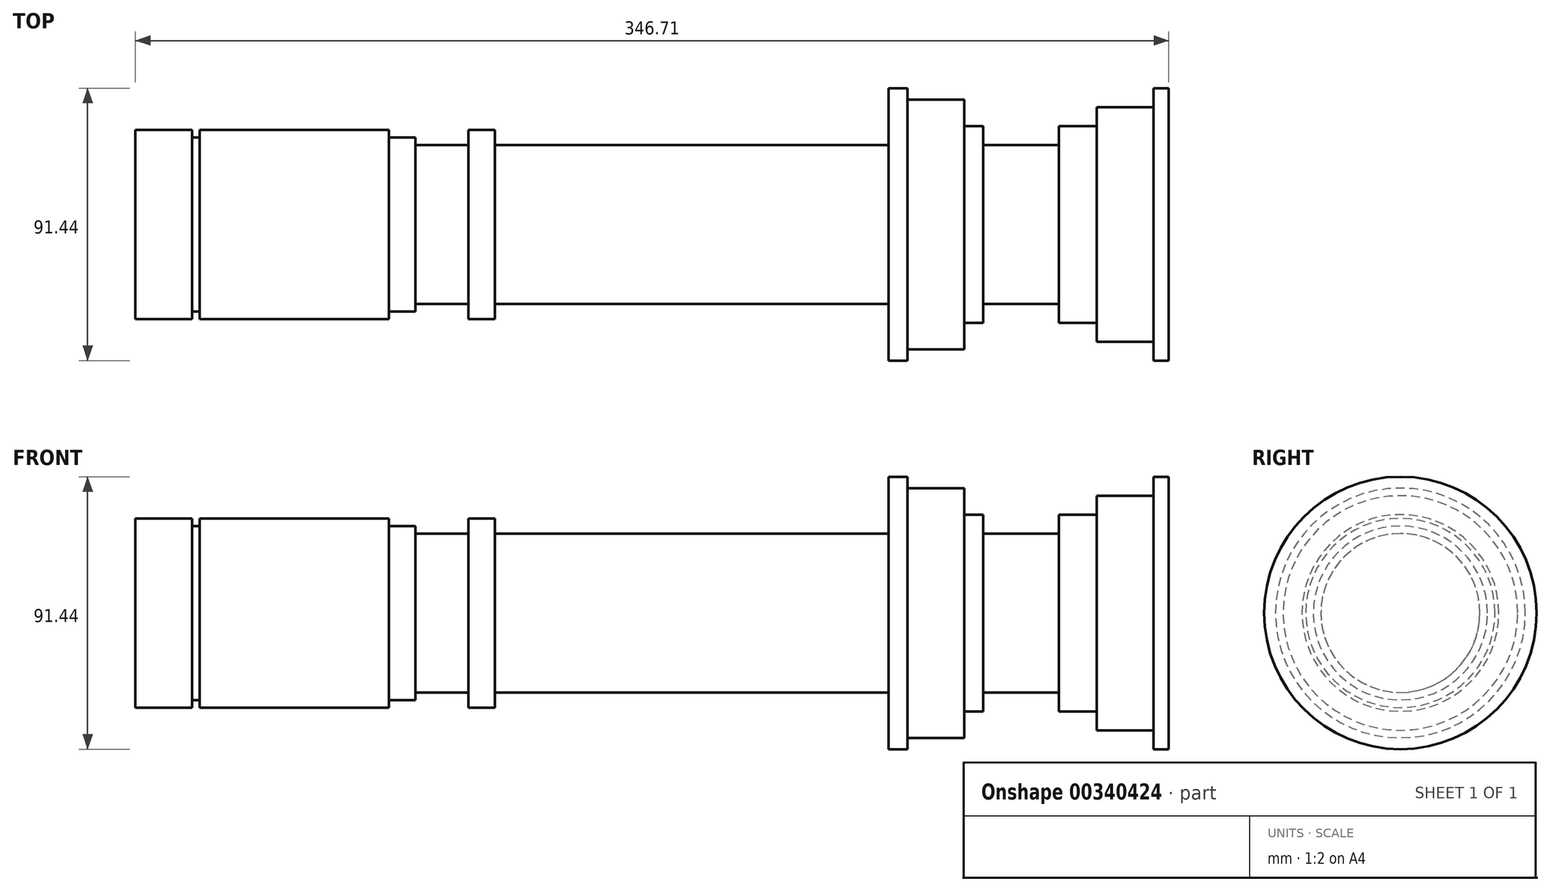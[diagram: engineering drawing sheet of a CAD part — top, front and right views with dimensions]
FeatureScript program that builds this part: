
annotation { "Feature Type Name" : "Feature", "Feature Type Description" : "" }
export const myFeature = defineFeature(function(context is Context, id is Id, definition is map)
    precondition{}
    {
        {
            var Q0;
            Q0=qCreatedBy(makeId("Front.planeOp"),FACE);
            var sketch = newSketch(context, id + "F0", { "sketchPlane" : qUnion([Q0])});
            skLineSegment(sketch, "E0", {"start": v(0, 31.75) * mm, "end": v(19.05, 31.75) * mm});
            skLineSegment(sketch, "E1", {"start": v(19.05, 31.75) * mm, "end": v(19.05, 29.21) * mm});
            skLineSegment(sketch, "E2", {"start": v(19.05, 29.21) * mm, "end": v(21.6, 29.21) * mm});
            skLineSegment(sketch, "E3", {"start": v(21.59, 29.21) * mm, "end": v(21.59, 31.75) * mm});
            skLineSegment(sketch, "E4", {"start": v(21.6, 31.75) * mm, "end": v(85.1, 31.75) * mm});
            skLineSegment(sketch, "E5", {"start": v(85.1, 31.75) * mm, "end": v(85.1, 29.21) * mm});
            skLineSegment(sketch, "E6", {"start": v(85.1, 29.21) * mm, "end": v(93.98, 29.21) * mm});
            skLineSegment(sketch, "E7", {"start": v(93.98, 29.21) * mm, "end": v(93.98, 26.67) * mm});
            skLineSegment(sketch, "E8", {"start": v(93.98, 26.67) * mm, "end": v(100.33, 26.67) * mm});
            skLineSegment(sketch, "E9", {"start": v(259.08, 45.72) * mm, "end": v(252.73, 45.72) * mm});
            skLineSegment(sketch, "E10", {"start": v(259.08, 41.9) * mm, "end": v(259.08, 45.72) * mm});
            skLineSegment(sketch, "E11", {"start": v(259.08, 41.9) * mm, "end": v(278.13, 41.9) * mm});
            skLineSegment(sketch, "E12", {"start": v(278.13, 41.9) * mm, "end": v(278.13, 33.02) * mm});
            skLineSegment(sketch, "E13", {"start": v(278.13, 33.02) * mm, "end": v(284.48, 33.02) * mm});
            skLineSegment(sketch, "E14", {"start": v(284.48, 33.02) * mm, "end": v(284.48, 26.67) * mm});
            skLineSegment(sketch, "E15", {"start": v(284.48, 26.67) * mm, "end": v(309.88, 26.67) * mm});
            skLineSegment(sketch, "E16", {"start": v(309.88, 26.67) * mm, "end": v(309.88, 33.02) * mm});
            skLineSegment(sketch, "E17", {"start": v(309.88, 33.02) * mm, "end": v(322.58, 33.02) * mm});
            skLineSegment(sketch, "E18", {"start": v(322.58, 33.02) * mm, "end": v(322.58, 39.37) * mm});
            skLineSegment(sketch, "E19", {"start": v(322.58, 39.37) * mm, "end": v(341.63, 39.37) * mm});
            skLineSegment(sketch, "E20", {"start": v(341.63, 39.37) * mm, "end": v(341.63, 45.72) * mm});
            skLineSegment(sketch, "E21", {"start": v(341.63, 45.72) * mm, "end": v(346.71, 45.72) * mm});
            skLineSegment(sketch, "E22", {"start": v(346.71, 45.72) * mm, "end": v(346.71, 0) * mm});
            skLineSegment(sketch, "E23", {"start": v(346.7, 0) * mm, "end": v(0, 0) * mm});
            skLineSegment(sketch, "E24", {"start": v(0, 0) * mm, "end": v(0, 31.75) * mm});
            skPoint(sketch, "E25.endSnap0", {"position": v(252.73, 39.77) * mm});
            skPoint(sketch, "E26.orphan", {"position": v(252.73, 33.82) * mm});
            skPoint(sketch, "E27.start.orphan", {"position": v(252.73, 48.82) * mm});
            skLineSegment(sketch, "E28", {"start": v(100.33, 26.67) * mm, "end": v(252.73, 26.67) * mm});
            skLineSegment(sketch, "E29", {"start": v(252.73, 45.72) * mm, "end": v(252.73, 26.67) * mm});
            skSolve(sketch);
        }
        {
            var Q0;
            Q0=makeQuery(id+"F0.imprint","IMPRINT",FACE,{"disambiguationData":[TD([[makeQuery(id+"F0.imprint","IMPRINT",EDGE,{"derivedFrom":sQuery(id+"F0.wireOp",EDGE,"E0")}),-1.0]])]});
            var Q1;
            Q1=sQuery(id+"F0.wireOp",EDGE,"E23");
            revolve(context, id + "F1", {"entities" : qUnion([Q0]), "axis" : qUnion([Q1]), "revolveType" : RevolveType.FULL});
        }
        {
            var Q0;
            Q0=qCreatedBy(makeId("Front.planeOp"),FACE);
            var sketch = newSketch(context, id + "F2", { "sketchPlane" : qUnion([Q0])});
            skLineSegment(sketch, "E30", {"start": v(0, 26.67) * mm, "end": v(254, 26.67) * mm});
            skLineSegment(sketch, "E31", {"start": v(0, 26.67) * mm, "end": v(0, 0) * mm});
            skLineSegment(sketch, "E32", {"start": v(111.76, 26.67) * mm, "end": v(111.76, 31.75) * mm});
            skLineSegment(sketch, "E33", {"start": v(111.76, 31.75) * mm, "end": v(120.65, 31.75) * mm});
            skLineSegment(sketch, "E34", {"start": v(120.65, 31.75) * mm, "end": v(120.65, 26.67) * mm});
            skLineSegment(sketch, "E35", {"start": v(100.33, 0) * mm, "end": v(157.12, 0) * mm});
            skLineSegment(sketch, "E36", {"start": v(111.76, 26.67) * mm, "end": v(105.41, 26.67) * mm});
            skLineSegment(sketch, "E37", {"start": v(127, 26.67) * mm, "end": v(127, 31.75) * mm});
            skLineSegment(sketch, "E38", {"start": v(127, 31.75) * mm, "end": v(139.7, 31.75) * mm});
            skLineSegment(sketch, "E39", {"start": v(139.7, 31.75) * mm, "end": v(139.7, 26.67) * mm});
            skLineSegment(sketch, "E40", {"start": v(139.7, 26.67) * mm, "end": v(148.92, 26.67) * mm});
            skLineSegment(sketch, "E41", {"start": v(148.92, 26.67) * mm, "end": v(148.92, 31.58) * mm});
            skLineSegment(sketch, "E42", {"start": v(148.92, 31.58) * mm, "end": v(158.79, 31.58) * mm});
            skLineSegment(sketch, "E43", {"start": v(158.79, 31.58) * mm, "end": v(158.79, 26.67) * mm});
            skLineSegment(sketch, "E44", {"start": v(158.79, 26.67) * mm, "end": v(170.18, 26.67) * mm});
            skLineSegment(sketch, "E45", {"start": v(170.18, 26.67) * mm, "end": v(170.18, 31.58) * mm});
            skLineSegment(sketch, "E46", {"start": v(170.18, 31.58) * mm, "end": v(181.28, 31.58) * mm});
            skLineSegment(sketch, "E47", {"start": v(181.28, 31.58) * mm, "end": v(181.28, 26.67) * mm});
            skLineSegment(sketch, "E48", {"start": v(0, 0) * mm, "end": v(100.33, 0) * mm});
            skSolve(sketch);
        }
        {
            var Q0;
            {var subQ0=sQuery(id+"F2.wireOp",EDGE,"E32");Q0=makeQuery(id+"F2.imprint","IMPRINT",FACE,{"disambiguationData":[TD([[makeQuery(id+"F2.imprint","IMPRINT",EDGE,{"derivedFrom":subQ0}),-1.0]])]});}
            var Q1;
            Q1=sQuery(id+"F0.wireOp",EDGE,"E23");
            revolve(context, id + "F3", {"operationType" : NewBodyOperationType.ADD, "entities" : qUnion([Q0]), "axis" : qUnion([Q1]), "revolveType" : RevolveType.FULL});
        }
    });
